# Revit family: Storage-Vessel_AO_Smith-ST-1500_F
name_source: partatom
category: Mechanical Equipment
revit_build: Autodesk Revit 2016 (Build: 20170117_1200(x64)
units: mm (PartAtom-declared; Revit-internal decimal feet)

## family parameters
Always vertical = Yes
Cut with Voids When Loaded = No
OmniClass Number = 23.75.00.00
OmniClass Title = Climate Control (HVAC)
Part Type = Normal
Room Calculation Point = No
Round Connector Dimension = Use Radius
Shared = No
Work Plane-Based = No

## types (1)
- Storage-Vessel_AO_Smith-ST-1500_F
    1er Entretien (check-up) = 3 mois après l'installation
    2ème Entretien (Entretien Général) = 12 mois après l'installation
    Assembly Code = D3010
    BIM Content Developer = CAD & Company
    BIM Content Developer URL = http://www.cadcompany.nl
    Capacité - Cuve = 1550 m³
    Charge Maximale au Sol = 1875.00 kg
    Description = Ballon de Stockage
    Destination / Pays = France
    Diamètre (avec Isolation) = 1300 mm  [stored 4.26509 ft]
    Diamètre (sans Isolation) = 1100 mm  [stored 3.60892 ft]
    Epaisseur d'Isolation = 100 mm  [stored 0.328084 ft]
    Fabricant No. = E 7110
    Garantie Pièces = 12 mois
    Garantie sur la Cuve = 36 mois
    Guide de Produit = https://www.aosmithinternational.com
    Hauteur (avec Isolation) = 1985 mm  [stored 6.51247 ft]
    Hauteur (sans Isolation) = 1985 mm  [stored 6.51247 ft]
    Hauteur d'Emballage = 2060 mm  [stored 6.75853 ft]
    Hauteur de l'Alimentation en eau Froide = 135 mm  [stored 0.442913 ft]
    Hauteur de la Sortie d'eau Chaude = 1985 mm  [stored 6.51247 ft]
    Largeur d'Emballage = 1170 mm  [stored 3.83858 ft]
    Manufacturer = A.O. Smith Water Products Company b.v.
    Max. Température de l'eau - Réservoir = 95 °C
    Model = ST 1500 F
    Nombre de modèle du produit (EAN) = 8717449172237
    Poids de Transport = 415.00 kg
    Poids à vide = 325.00 kg
    Pression de Service Maximale - Réservoir = 1000000.0 Pa
    Profondeur d'Emballage = 1426 mm
    Raccord d'Alimentation en Eau Froide = 2"
    Raccord de Sortie d'Eau Chaude = 2"
    Raccord de la Soupape de Vidange = 2"
    Spécifications du Produit = https://www.aosmithinternational.com
    Type d'Emballage = Plastique et Bois
    URL = http://www.aosmith.fr
    Workspace Diameter = 2300 mm
    Workspace Height = 2985 mm
    espace de travail = 1100 mm  [stored 3.60892 ft]
    l'Intervalle d'Entretien = 12 mois

note: [stored X ft] marks values corroborated as IEEE doubles in the binary element streams (Revit-internal decimal feet)

## geometry (parser evidence)
native form markers: Blend x2, Sweep x13
no freeform markers — native parametric forms only
